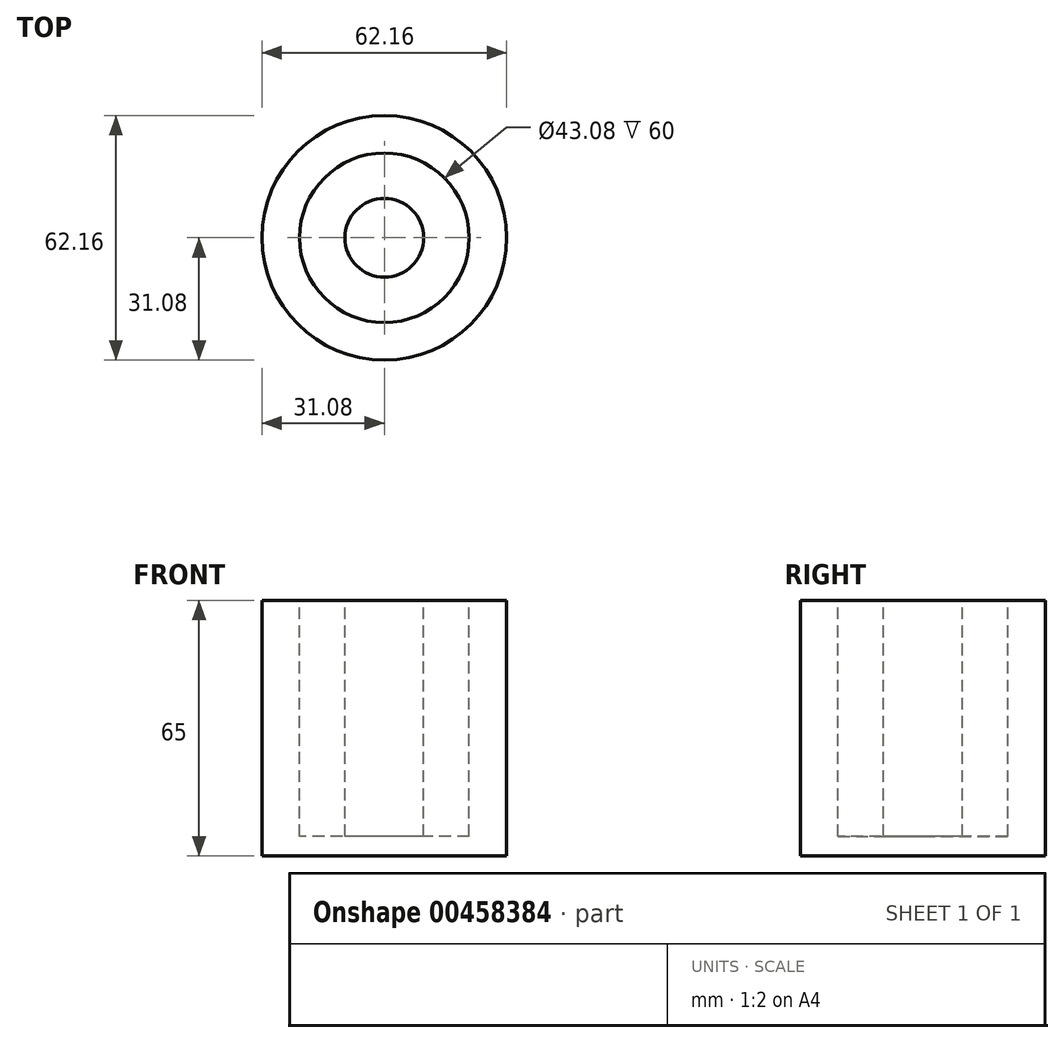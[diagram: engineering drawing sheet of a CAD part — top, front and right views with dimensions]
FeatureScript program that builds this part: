
annotation { "Feature Type Name" : "Feature", "Feature Type Description" : "" }
export const myFeature = defineFeature(function(context is Context, id is Id, definition is map)
    precondition{}
    {
        {
            var Q0;
            Q0=qCreatedBy(makeId("Top.planeOp"),FACE);
            var sketch = newSketch(context, id + "F0", { "sketchPlane" : qUnion([Q0])});
            skCircle(sketch, "E0", {"center": v(0, 0) * mm, "radius": 31.08 * mm});
            skSolve(sketch);
        }
        {
            var Q0;
            Q0=makeQuery(id+"F0.imprint","IMPRINT",FACE,{"disambiguationData":[TD([[makeQuery(id+"F0.imprint","IMPRINT",EDGE,{"derivedFrom":sQuery(id+"F0.wireOp",EDGE,"E0")}),1.0]])]});
            extrude(context, id + "F1", {"entities" : qUnion([Q0]), "offsetDistance" : 25 * mm, "depth" : 65 * mm});
        }
        {
            var Q0;
            Q0=makeQuery(id+"F1.opExtrude","CAP_FACE",FACE,{"disambiguationData":[OSD([sQuery(id+"F0.wireOp",EDGE,"E0")])],"isStart":false});
            var sketch = newSketch(context, id + "F2", { "sketchPlane" : qUnion([Q0])});
            skCircle(sketch, "E1", {"center": v(0, 0) * mm, "radius": 21.54 * mm});
            skCircle(sketch, "E2", {"center": v(0, 0) * mm, "radius": 10 * mm});
            skSolve(sketch);
        }
        {
            var Q0;
            Q0=makeQuery(id+"F2.imprint","IMPRINT",FACE,{"disambiguationData":[TD([[makeQuery(id+"F2.imprint","IMPRINT",EDGE,{"derivedFrom":sQuery(id+"F2.wireOp",EDGE,"E1")}),1.0]])]});
            extrude(context, id + "F3", {"entities" : qUnion([Q0]), "operationType" : NewBodyOperationType.REMOVE, "oppositeDirection" : true, "offsetDistance" : 25 * mm, "depth" : 60 * mm});
        }
        {
            var Q0;
            Q0=qCreatedBy(makeId("Top.planeOp"),FACE);
            cPlane(context, id + "F4", {"entities" : qUnion([Q0]), "cplaneType" : CPlaneType.OFFSET, "offset" : 30 * mm, "width" : 150 * mm, "height" : 150 * mm});
        }
        {
            var Q0;
            Q0=qCreatedBy(makeId("Right.planeOp"),FACE);
            cPlane(context, id + "F5", {"entities" : qUnion([Q0]), "cplaneType" : CPlaneType.OFFSET, "offset" : 100 * mm, "oppositeDirection" : true, "width" : 150 * mm, "height" : 150 * mm});
        }
        {
            var Q0;
            Q0=qCreatedBy(makeId("Front.planeOp"),FACE);
            cPlane(context, id + "F6", {"entities" : qUnion([Q0]), "cplaneType" : CPlaneType.OFFSET, "offset" : 27 * mm, "oppositeDirection" : true, "width" : 150 * mm, "height" : 150 * mm});
        }
    });
